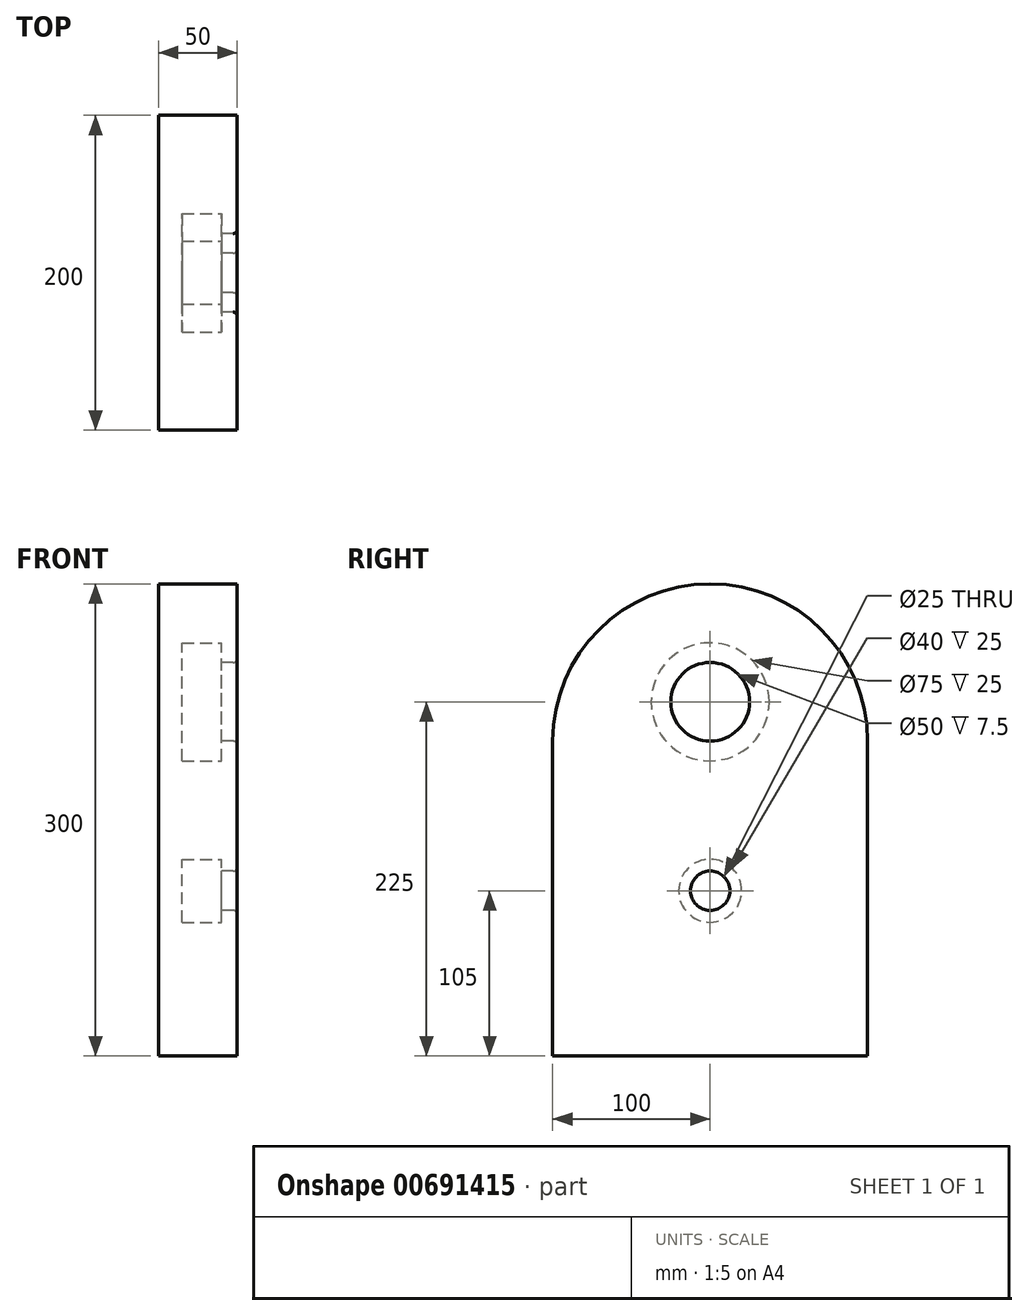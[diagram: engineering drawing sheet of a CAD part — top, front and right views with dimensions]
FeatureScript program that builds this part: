
annotation { "Feature Type Name" : "Feature", "Feature Type Description" : "" }
export const myFeature = defineFeature(function(context is Context, id is Id, definition is map)
    precondition{}
    {
        {
            var Q0;
            Q0=qCreatedBy(makeId("Right.planeOp"),FACE);
            var sketch = newSketch(context, id + "F0", { "sketchPlane" : qUnion([Q0])});
            skLineSegment(sketch, "E0.top", {"start": v(100, -100) * mm, "end": v(-100, -100) * mm});
            skLineSegment(sketch, "E0.left", {"start": v(100, 100) * mm, "end": v(100, -100) * mm});
            skLineSegment(sketch, "E0.right", {"start": v(-100, 100) * mm, "end": v(-100, -100) * mm});
            skPoint(sketch, "E0.middle", {"position": v(0, 0) * mm});
            skArc(sketch, "E1", {"start": v(100, 100) * mm, "mid": v(0, 200) * mm, "end": v(-100, 100) * mm});
            skSolve(sketch);
        }
        {
            var Q0;
            Q0 = qSketchRegion(id + "F0", true);
            extrude(context, id + "F1", {"entities" : qUnion([Q0]), "depth" : 40 * mm, "offsetDistance" : 25 * mm});
        }
        {
            var Q0;
            Q0=makeQuery(id+"F1.opExtrude","CAP_FACE",FACE,{"disambiguationData":[OSD([sQuery(id+"F0.wireOp",EDGE,"E0.top"),sQuery(id+"F0.wireOp",EDGE,"E0.left"),sQuery(id+"F0.wireOp",EDGE,"E0.right"),sQuery(id+"F0.wireOp",EDGE,"E1")])],"isStart":false});
            var sketch = newSketch(context, id + "F2", { "sketchPlane" : qUnion([Q0])});
            skCircle(sketch, "E2", {"center": v(0, 125) * mm, "radius": 37.5 * mm});
            skCircle(sketch, "E3", {"center": v(0, 5) * mm, "radius": 20 * mm});
            skSolve(sketch);
        }
        {
            var Q0;
            Q0=makeQuery(id+"F1.opExtrude","CAP_FACE",FACE,{"disambiguationData":[OSD([sQuery(id+"F0.wireOp",EDGE,"E0.top"),sQuery(id+"F0.wireOp",EDGE,"E0.left"),sQuery(id+"F0.wireOp",EDGE,"E0.right"),sQuery(id+"F0.wireOp",EDGE,"E1")])],"isStart":false});
            var sketch = newSketch(context, id + "F3", { "sketchPlane" : qUnion([Q0])});
            skLineSegment(sketch, "E4.bottom", {"start": v(100, -100) * mm, "end": v(-100, -100) * mm});
            skLineSegment(sketch, "E4.left", {"start": v(100, -100) * mm, "end": v(100, 100) * mm});
            skLineSegment(sketch, "E4.right", {"start": v(-100, -100) * mm, "end": v(-100, 100) * mm});
            skPoint(sketch, "E4.middle", {"position": v(0, 0) * mm});
            skArc(sketch, "E5", {"start": v(100, 100) * mm, "mid": v(0, 200) * mm, "end": v(-100, 100) * mm});
            skSolve(sketch);
        }
        {
            var Q0;
            Q0=makeQuery(id+"F2.imprint","IMPRINT",FACE,{"disambiguationData":[TD([[makeQuery(id+"F2.imprint","IMPRINT",EDGE,{"derivedFrom":sQuery(id+"F2.wireOp",EDGE,"E2")}),1.0]])]});
            var Q1;
            Q1=makeQuery(id+"F2.imprint","IMPRINT",FACE,{"disambiguationData":[TD([[makeQuery(id+"F2.imprint","IMPRINT",EDGE,{"derivedFrom":sQuery(id+"F2.wireOp",EDGE,"E3")}),1.0]])]});
            extrude(context, id + "F4", {"entities" : qUnion([Q0, Q1]), "operationType" : NewBodyOperationType.REMOVE, "oppositeDirection" : true, "depth" : 25 * mm, "offsetDistance" : 25 * mm});
        }
        {
            var Q0;
            Q0=makeQuery(id+"F3.imprint","IMPRINT",FACE,{"disambiguationData":[TD([[makeQuery(id+"F3.imprint","IMPRINT",EDGE,{"derivedFrom":sQuery(id+"F3.wireOp",EDGE,"E4.bottom")}),-1.0]])]});
            var sketch = newSketch(context, id + "F5", { "sketchPlane" : qUnion([Q0])});
            skLineSegment(sketch, "E6.top", {"start": v(100, -100) * mm, "end": v(-100, -100) * mm});
            skLineSegment(sketch, "E6.left", {"start": v(100, 100) * mm, "end": v(100, -100) * mm});
            skLineSegment(sketch, "E6.right", {"start": v(-100, 100) * mm, "end": v(-100, -100) * mm});
            skPoint(sketch, "E6.middle", {"position": v(0, 0) * mm});
            skArc(sketch, "E7", {"start": v(100, 100) * mm, "mid": v(0, 200) * mm, "end": v(-100, 100) * mm});
            skCircle(sketch, "E8", {"center": v(0, 125) * mm, "radius": 25 * mm});
            skCircle(sketch, "E9", {"center": v(0, 5) * mm, "radius": 12.5 * mm});
            skSolve(sketch);
        }
        {
            var Q0;
            Q0 = qSketchRegion(id + "F5", true);
            extrude(context, id + "F6", {"entities" : qUnion([Q0]), "operationType" : NewBodyOperationType.ADD, "depth" : 10 * mm, "offsetDistance" : 25 * mm});
        }
        {
            var Q0;
            Q0=makeQuery(id+"F6.opExtrude","CAP_EDGE",EDGE,{"disambiguationData":[OSD([sQuery(id+"F5.wireOp",EDGE,"E8")])],"isStart":false});
            var Q1;
            Q1=makeQuery(id+"F6.opExtrude","CAP_EDGE",EDGE,{"disambiguationData":[OSD([sQuery(id+"F5.wireOp",EDGE,"E9")])],"isStart":false});
            fillet(context, id + "F7", {"entities" : qUnion([Q0, Q1]), "radius" : 2.5 * mm, "tangentPropagation" : true, "allowEdgeOverflow" : false});
        }
    });
